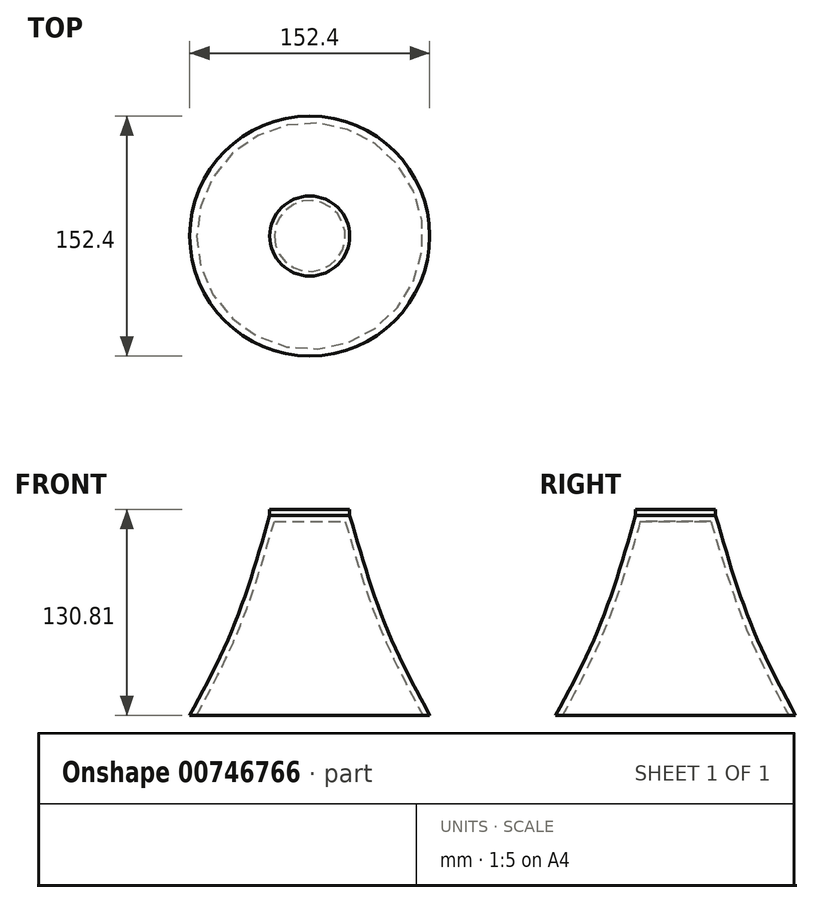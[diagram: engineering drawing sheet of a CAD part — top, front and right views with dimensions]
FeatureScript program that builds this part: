
annotation { "Feature Type Name" : "Feature", "Feature Type Description" : "" }
export const myFeature = defineFeature(function(context is Context, id is Id, definition is map)
    precondition{}
    {
        {
            var Q0;
            Q0=qCreatedBy(makeId("Top.planeOp"),FACE);
            var sketch = newSketch(context, id + "F0", { "sketchPlane" : qUnion([Q0])});
            skCircle(sketch, "E0", {"center": v(0, 0) * mm, "radius": 76.2 * mm});
            skSolve(sketch);
        }
        {
            var Q0;
            Q0=qCreatedBy(makeId("Top.planeOp"),FACE);
            cPlane(context, id + "F1", {"entities" : qUnion([Q0]), "cplaneType" : CPlaneType.OFFSET, "offset" : 50.8 * mm, "width" : 152.4 * mm, "height" : 152.4 * mm});
        }
        {
            var Q0;
            Q0=qCreatedBy(id+"F1.planeOp",FACE);
            var sketch = newSketch(context, id + "F2", { "sketchPlane" : qUnion([Q0])});
            skCircle(sketch, "E1", {"center": v(0, 0) * mm, "radius": 50.8 * mm});
            skSolve(sketch);
        }
        {
            var Q0;
            Q0=qCreatedBy(id+"F1.planeOp",FACE);
            var Q1;
            Q1 = qBodyType(qCreatedBy(id + "F4" ,EDGE), BodyType.WIRE);
            cPlane(context, id + "F3", {"entities" : qUnion([Q0, Q1]), "cplaneType" : CPlaneType.OFFSET, "offset" : 76.2 * mm, "width" : 152.4 * mm, "height" : 152.4 * mm});
        }
        {
            var Q0;
            Q0=qCreatedBy(id+"F3.planeOp",FACE);
            var sketch = newSketch(context, id + "F4", { "sketchPlane" : qUnion([Q0])});
            skCircle(sketch, "E2", {"center": v(0, 0) * mm, "radius": 25.4 * mm});
            skSolve(sketch);
        }
        {
            var Q0;
            Q0=makeQuery(id+"F0.imprint","IMPRINT",FACE,{"disambiguationData":[TD([[makeQuery(id+"F0.imprint","IMPRINT",EDGE,{"derivedFrom":sQuery(id+"F0.wireOp",EDGE,"E0")}),1.0]])]});
            var Q1;
            Q1=makeQuery(id+"F2.imprint","IMPRINT",FACE,{"disambiguationData":[TD([[makeQuery(id+"F2.imprint","IMPRINT",EDGE,{"derivedFrom":sQuery(id+"F2.wireOp",EDGE,"E1")}),1.0]])]});
            var Q2;
            Q2=makeQuery(id+"F4.imprint","IMPRINT",FACE,{"disambiguationData":[TD([[makeQuery(id+"F4.imprint","IMPRINT",EDGE,{"derivedFrom":sQuery(id+"F4.wireOp",EDGE,"E2")}),1.0]])]});
            loft(context, id + "F5", {"sheetProfilesArray" : [{ "sheetProfileEntities" : qUnion([Q0]) }, { "sheetProfileEntities" : qUnion([Q1]) }, { "sheetProfileEntities" : qUnion([Q2]) }]});
        }
        {
            var Q0;
            Q0=makeQuery(id+"F5.opLoft","CAP_FACE",FACE,{"disambiguationData":[OSD([makeQuery(id+"F0.imprint","IMPRINT",FACE,{"disambiguationData":[TD([[makeQuery(id+"F0.imprint","IMPRINT",EDGE,{"derivedFrom":sQuery(id+"F0.wireOp",EDGE,"E0")}),1.0]])]})])],"isStart":true});
            shell(context, id + "F6", {"entities" : qUnion([Q0]), "thickness" : 3.8 * mm});
        }
        {
            var Q0;
            Q0=makeQuery(id+"F4.imprint","IMPRINT",FACE,{"disambiguationData":[TD([[makeQuery(id+"F4.imprint","IMPRINT",EDGE,{"derivedFrom":sQuery(id+"F4.wireOp",EDGE,"E2")}),1.0]])]});
            extrude(context, id + "F7", {"entities" : qUnion([Q0]), "depth" : 3.8 * mm, "offsetDistance" : 25.4 * mm});
        }
    });
